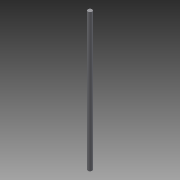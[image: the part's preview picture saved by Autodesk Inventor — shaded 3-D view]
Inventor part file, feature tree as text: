
AUTODESK INVENTOR PART (.ipt)
format: ipt  version: 2013 (Build 170138000, 138)  size: 59,904 bytes
history: native  units: in
note: dims shown in document units (in); Inventor stores cm internally (conversion verified against a paired STEP export)
features: extrude x1, sketch x1
ambient origin geometry x8: Origin, YZ Plane, XZ Plane, XY Plane, X Axis, Y Axis, Z Axis, Center Point
bodies: Solid1 (feature_tree)
feature tree (2):
  extrude  "Extrusion1"  Depth=16.25in TaperAngle=0.0deg
  sketch  "Sketch1"  dims[d0=0.5in d1=16.25in d2=0.0in]
